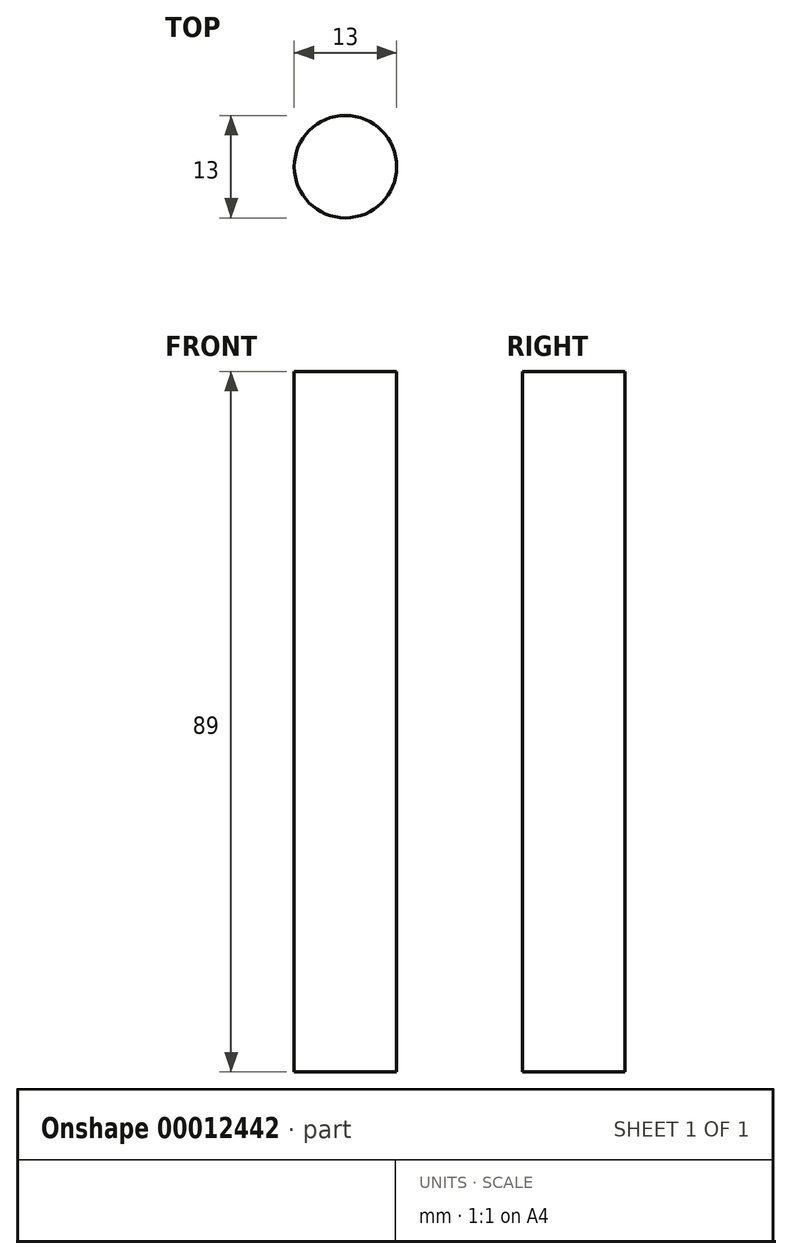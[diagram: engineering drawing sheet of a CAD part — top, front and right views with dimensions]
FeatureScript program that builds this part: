
annotation { "Feature Type Name" : "Feature", "Feature Type Description" : "" }
export const myFeature = defineFeature(function(context is Context, id is Id, definition is map)
    precondition{}
    {
        {
            var Q0;
            Q0=qCreatedBy(makeId("Top.planeOp"),FACE);
            var sketch = newSketch(context, id + "F0", { "sketchPlane" : qUnion([Q0])});
            skCircle(sketch, "E0", {"center": v(-36.53, 13.4) * mm, "radius": 6.5 * mm});
            skSolve(sketch);
        }
        {
            var Q0;
            Q0 = qSketchRegion(id + "F0", true);
            extrude(context, id + "F1", {"entities" : qUnion([Q0]), "depth" : 89 * mm});
        }
    });
